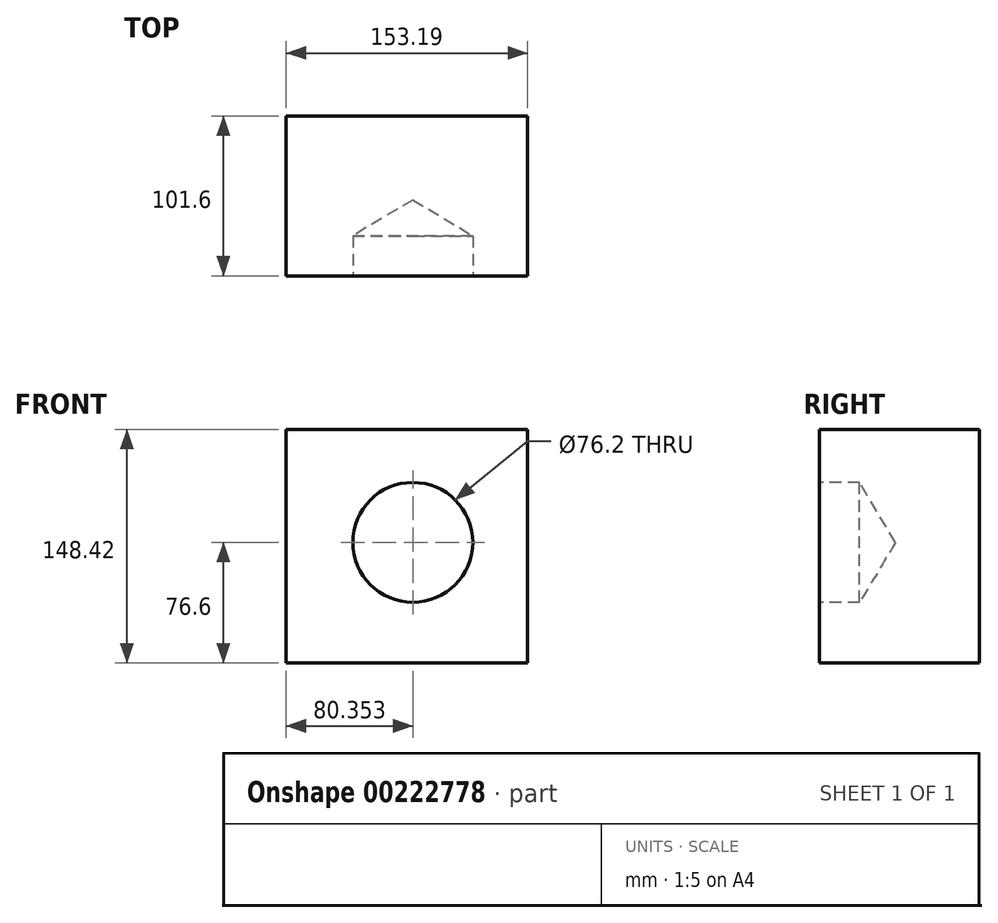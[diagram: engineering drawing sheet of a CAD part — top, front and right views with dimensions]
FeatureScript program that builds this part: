
annotation { "Feature Type Name" : "Feature", "Feature Type Description" : "" }
export const myFeature = defineFeature(function(context is Context, id is Id, definition is map)
    precondition{}
    {
        {
            var Q0;
            Q0=qCreatedBy(makeId("Front.planeOp"),FACE);
            var sketch = newSketch(context, id + "F0", { "sketchPlane" : qUnion([Q0])});
            skLineSegment(sketch, "E0.bottom", {"start": v(-74.89, 71.82) * mm, "end": v(78.3, 71.82) * mm});
            skLineSegment(sketch, "E0.top", {"start": v(-74.89, -76.6) * mm, "end": v(78.3, -76.6) * mm});
            skLineSegment(sketch, "E0.left", {"start": v(-74.89, 71.82) * mm, "end": v(-74.89, -76.6) * mm});
            skLineSegment(sketch, "E0.right", {"start": v(78.3, 71.82) * mm, "end": v(78.3, -76.6) * mm});
            skPoint(sketch, "E1", {"position": v(5, 0) * mm});
            skSolve(sketch);
        }
        {
            var Q0;
            Q0=makeQuery(id+"F0.imprint","IMPRINT",FACE,{"disambiguationData":[TD([[makeQuery(id+"F0.imprint","IMPRINT",EDGE,{"derivedFrom":sQuery(id+"F0.wireOp",EDGE,"E0.bottom")}),-1.0]])]});
            extrude(context, id + "F1", {"entities" : qUnion([Q0]), "depth" : 101.6 * mm});
        }
        {
            var Q0;
            Q0=makeQuery(id+"F1.opExtrude","CAP_FACE",FACE,{"disambiguationData":[OSD([sQuery(id+"F0.wireOp",EDGE,"E0.bottom"),sQuery(id+"F0.wireOp",EDGE,"E0.top"),sQuery(id+"F0.wireOp",EDGE,"E0.left"),sQuery(id+"F0.wireOp",EDGE,"E0.right")])],"isStart":false});
            var sketch = newSketch(context, id + "F2", { "sketchPlane" : qUnion([Q0])});
            skPoint(sketch, "E2", {"position": v(5.46, 0) * mm});
            skSolve(sketch);
        }
        {
            var Q0;
            Q0=sQuery(id+"F2.wireOp",VERTEX,"E2");
            var Q1;
            Q1=makeQuery(id+"F1.opExtrude","SWEPT_BODY",BODY,{"disambiguationData":[OSD([sQuery(id+"F0.wireOp",EDGE,"E0.bottom"),sQuery(id+"F0.wireOp",EDGE,"E0.top"),sQuery(id+"F0.wireOp",EDGE,"E0.left"),sQuery(id+"F0.wireOp",EDGE,"E0.right")])]});
            hole(context, id + "F3", {"style" : HoleStyle.SIMPLE, "endStyle" : HoleEndStyle.BLIND, "holeDiameter" : 76.2 * mm, "holeDepth" : 25.4 * mm, "locations" : qUnion([Q0]), "scope" : qUnion([Q1])});
        }
    });
